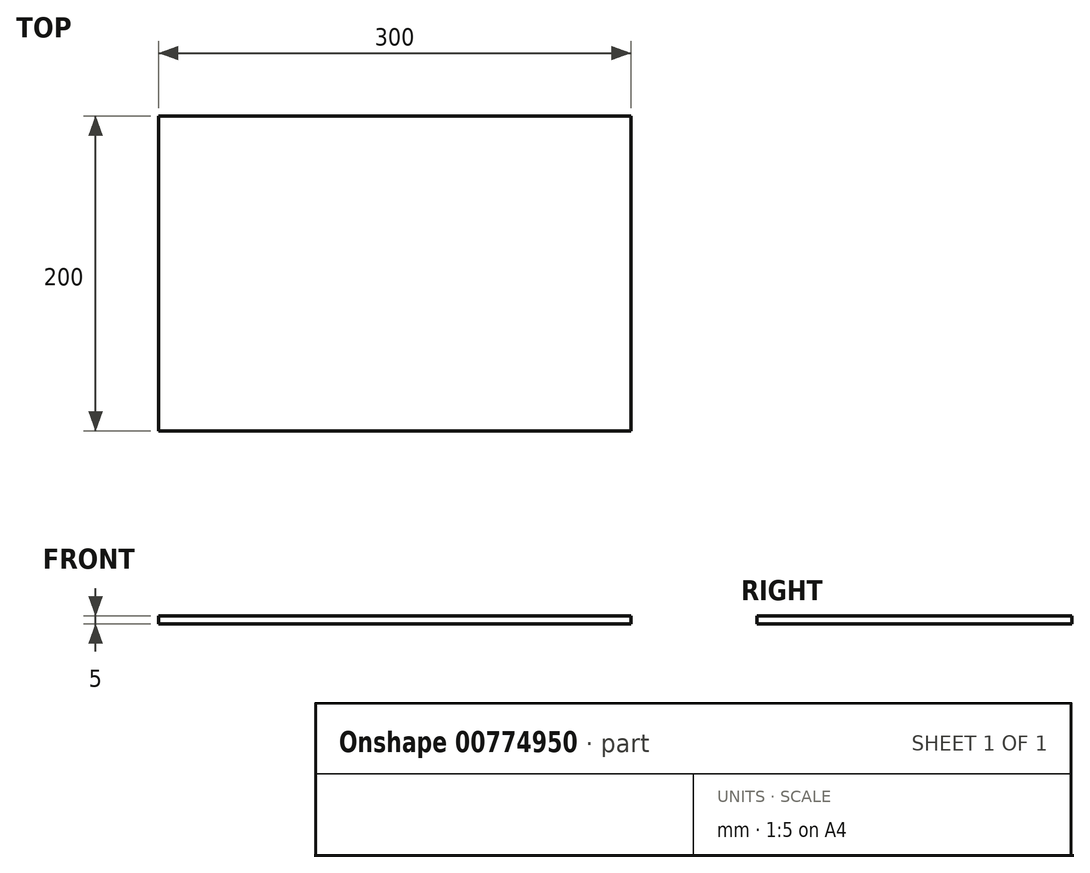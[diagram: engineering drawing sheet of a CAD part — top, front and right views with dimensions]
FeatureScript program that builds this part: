
annotation { "Feature Type Name" : "Feature", "Feature Type Description" : "" }
export const myFeature = defineFeature(function(context is Context, id is Id, definition is map)
    precondition{}
    {
        {
            var Q0;
            Q0=qCreatedBy(makeId("Top.planeOp"),FACE);
            var sketch = newSketch(context, id + "F0", { "sketchPlane" : qUnion([Q0])});
            skLineSegment(sketch, "E0.bottom", {"start": v(-150, 100) * mm, "end": v(150, 100) * mm});
            skLineSegment(sketch, "E0.top", {"start": v(-150, -100) * mm, "end": v(150, -100) * mm});
            skLineSegment(sketch, "E0.left", {"start": v(-150, 100) * mm, "end": v(-150, -100) * mm});
            skLineSegment(sketch, "E0.right", {"start": v(150, 100) * mm, "end": v(150, -100) * mm});
            skPoint(sketch, "E0.middle", {"position": v(0, 0) * mm});
            skSolve(sketch);
        }
        {
            var Q0;
            Q0=makeQuery(id+"F0.imprint","IMPRINT",FACE,{"disambiguationData":[TD([[makeQuery(id+"F0.imprint","IMPRINT",EDGE,{"derivedFrom":sQuery(id+"F0.wireOp",EDGE,"E0.bottom")}),-1.0]])]});
            extrude(context, id + "F1", {"entities" : qUnion([Q0]), "depth" : 5 * mm, "offsetDistance" : 25 * mm});
        }
    });
